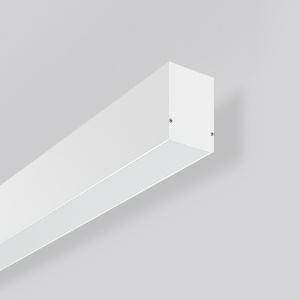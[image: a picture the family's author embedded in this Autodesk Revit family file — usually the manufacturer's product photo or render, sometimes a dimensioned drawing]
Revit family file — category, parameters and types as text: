
# Revit family: less_is_more_50_312610_002_1_2a81
name_source: partatom
category: Lighting Fixtures
units: mm (PartAtom-declared; Revit-internal decimal feet)

## family parameters
Cut with Voids When Loaded = No
Host = Face
Light Source = No
Part Type = Normal
Room Calculation Point = No
Round Connector Dimension = Use Diameter
Shared = No

## types (1)
- LESS IS MORE 50 (1 x LED Modul 840, 3400 lm, 4000)
    Apparent Load = 25 VA
    CIE Flux Codes = 48 80 96 50 100
    Color Rendering = 80
    Color Temperature = 4000
    Default Elevation = 1800 mm
    Description = Series: LESS IS MORE 50
Linear wall luminaires. Housing: extruded aluminium profile, powder-coated. End cap aluminium powder-coated. Diffuser made of non-yellowing plastic (PMMA), opal. Direct 50%, indirect 50% light emission. Suitable for Wall (surface). LED unit with integrated converter interchangeable and removable. Suitable for through-wiring. With sensors or as a safety luminaire on request. 
Colour: traffic white, matt (RAL 9016)
Length: 1407 mm
Width: 67 mm
Height: 75 mm
Lamp: LED
Socket: without socket
Colour temperature: 4000K
Colour rendering index (CRI): 80
Light source: LED
Socket lamp2: Without base
Colour temperature: 4000K
Colour rendering index (CRI) 2: 80
System power: 25 W
Rated luminous flux: 3400 lm
Luminous efficiency: 136 lm/W
Control gear: Regulated power supply
Control gear: Regulated power supply
Protection class: I
Type of protection: IP 20
    Height = 75 mm
    Lamp = 1 x LED Modul 840
    Lamp Light Flux = 3400 lm
    Lamp count = 1
    Length = 1407 mm
    Lifetime = 50000 h
    Luminous efficacy = 136 lm/W
    Manufacturer = RZB
    ModVariant = No
    Model = 312610.002.1
    Mounting Place = Wall
    Mounting Type = Surface mounted
    Number of Poles = 1
    OnlyDefault = Yes
    Power Factor = 1
    Product Name = LESS IS MORE 50
    Product group = Surface mounted LED linear luminaires
    ProductGroupID = 2007
    Protection Class = Protection class I
    Protection Degree = IP 20
    RLX_Detail_Level = 1
    RLX_Emergency_Light_Flux = 0 lm
    RLX_Emergency_Type = 0
    RLX_Emergency_Type_DB = No
    RlxData = <blob elided: 39593 chars, md5=d346174b>
    Socket = socket
    Standby Power = 0 W
    System Light Flux = 3400 lm
    System Power = 25 W
    Type Comments = Product without accessories
    Type Image = 312606.002.jpg
    URL = http://relux.com
    VarID = ---
    Voltage = 0 V
    Weight = 0.00 kg
    Width = 67 mm

## geometry (parser evidence)
native form markers: Blend x4, Sweep x12
no freeform markers — native parametric forms only
